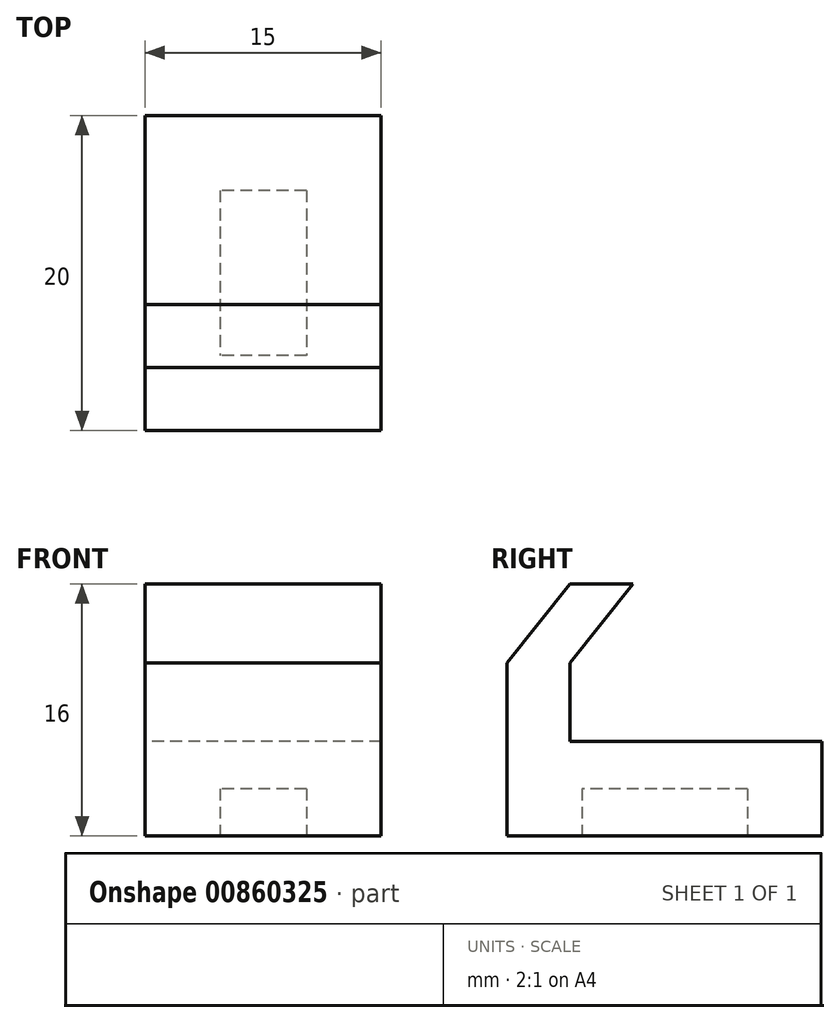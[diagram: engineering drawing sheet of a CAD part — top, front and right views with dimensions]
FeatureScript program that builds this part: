
annotation { "Feature Type Name" : "Feature", "Feature Type Description" : "" }
export const myFeature = defineFeature(function(context is Context, id is Id, definition is map)
    precondition{}
    {
        {
            var Q0;
            Q0=qCreatedBy(makeId("Top.planeOp"),FACE);
            var sketch = newSketch(context, id + "F0", { "sketchPlane" : qUnion([Q0])});
            skLineSegment(sketch, "E0.bottom", {"start": v(0, 0) * mm, "end": v(-15, 0) * mm});
            skLineSegment(sketch, "E0.top", {"start": v(0, 20) * mm, "end": v(-15, 20) * mm});
            skLineSegment(sketch, "E0.left", {"start": v(0, 0) * mm, "end": v(0, 20) * mm});
            skLineSegment(sketch, "E0.right", {"start": v(-15, 0) * mm, "end": v(-15, 20) * mm});
            skSolve(sketch);
        }
        {
            var Q0;
            Q0=makeQuery(id+"F0.imprint","IMPRINT",FACE,{"disambiguationData":[TD([[makeQuery(id+"F0.imprint","IMPRINT",EDGE,{"derivedFrom":sQuery(id+"F0.wireOp",EDGE,"E0.bottom")}),-1.0]])]});
            extrude(context, id + "F1", {"entities" : qUnion([Q0]), "depth" : 6 * mm, "offsetDistance" : 25 * mm});
        }
        {
            var Q0;
            Q0=makeQuery(id+"F1.opExtrude","CAP_FACE",FACE,{"disambiguationData":[OSD([sQuery(id+"F0.wireOp",EDGE,"E0.bottom"),sQuery(id+"F0.wireOp",EDGE,"E0.top"),sQuery(id+"F0.wireOp",EDGE,"E0.left"),sQuery(id+"F0.wireOp",EDGE,"E0.right")])],"isStart":true});
            var sketch = newSketch(context, id + "F2", { "sketchPlane" : qUnion([Q0])});
            skLineSegment(sketch, "E1.bottom", {"start": v(-4.75, -15.25) * mm, "end": v(-10.25, -15.25) * mm});
            skLineSegment(sketch, "E1.top", {"start": v(-4.75, -4.75) * mm, "end": v(-10.25, -4.75) * mm});
            skLineSegment(sketch, "E1.left", {"start": v(-4.75, -15.25) * mm, "end": v(-4.75, -4.75) * mm});
            skLineSegment(sketch, "E1.right", {"start": v(-10.25, -15.25) * mm, "end": v(-10.25, -4.75) * mm});
            skLineSegment(sketch, "E2", {"start": v(-7.5, 0) * mm, "end": v(-7.5, -4.75) * mm});
            skLineSegment(sketch, "E3", {"start": v(-7.5, -15.25) * mm, "end": v(-7.5, -20) * mm});
            skSolve(sketch);
        }
        {
            var Q0;
            {var subQ3=sQuery(id+"F2.wireOp",EDGE,"E1.left");Q0=makeQuery(id+"F2.imprint","IMPRINT",FACE,{"disambiguationData":[TD([[makeQuery(id+"F2.imprint","IMPRINT",EDGE,{"derivedFrom":subQ3}),1.0]])]});}
            extrude(context, id + "F3", {"entities" : qUnion([Q0]), "operationType" : NewBodyOperationType.REMOVE, "oppositeDirection" : true, "depth" : 3 * mm, "offsetDistance" : 25 * mm});
        }
        {
            var Q0;
            Q0=makeQuery(id+"F1.opExtrude","CAP_FACE",FACE,{"disambiguationData":[OSD([sQuery(id+"F0.wireOp",EDGE,"E0.bottom"),sQuery(id+"F0.wireOp",EDGE,"E0.top"),sQuery(id+"F0.wireOp",EDGE,"E0.left"),sQuery(id+"F0.wireOp",EDGE,"E0.right")])],"isStart":false});
            var sketch = newSketch(context, id + "F4", { "sketchPlane" : qUnion([Q0])});
            skLineSegment(sketch, "E4.bottom", {"start": v(0, 0) * mm, "end": v(-15, 0) * mm});
            skLineSegment(sketch, "E4.top", {"start": v(0, 4) * mm, "end": v(-15, 4) * mm});
            skLineSegment(sketch, "E4.left", {"start": v(0, 0) * mm, "end": v(0, 4) * mm});
            skLineSegment(sketch, "E4.right", {"start": v(-15, 0) * mm, "end": v(-15, 4) * mm});
            skSolve(sketch);
        }
        {
            var Q0;
            Q0=makeQuery(id+"F4.imprint","IMPRINT",FACE,{"disambiguationData":[TD([[makeQuery(id+"F4.imprint","IMPRINT",EDGE,{"derivedFrom":sQuery(id+"F4.wireOp",EDGE,"E4.bottom")}),-1.0]])]});
            extrude(context, id + "F5", {"entities" : qUnion([Q0]), "operationType" : NewBodyOperationType.ADD, "depth" : 5 * mm, "offsetDistance" : 25 * mm});
        }
        {
            var Q0;
            Q0=makeQuery(id+"F5.opExtrude","CAP_FACE",FACE,{"disambiguationData":[OSD([sQuery(id+"F4.wireOp",EDGE,"E4.bottom"),sQuery(id+"F4.wireOp",EDGE,"E4.top"),sQuery(id+"F4.wireOp",EDGE,"E4.left"),sQuery(id+"F4.wireOp",EDGE,"E4.right")])],"isStart":false});
            cPlane(context, id + "F6", {"entities" : qUnion([Q0]), "cplaneType" : CPlaneType.OFFSET, "offset" : 5 * mm, "width" : 150 * mm, "height" : 150 * mm});
        }
        {
            var Q0;
            Q0=qCreatedBy(id+"F6.planeOp",FACE);
            var sketch = newSketch(context, id + "F7", { "sketchPlane" : qUnion([Q0])});
            skLineSegment(sketch, "E5.bottom", {"start": v(0, 4) * mm, "end": v(-15, 4) * mm});
            skLineSegment(sketch, "E5.top", {"start": v(0, 8) * mm, "end": v(-15, 8) * mm});
            skLineSegment(sketch, "E5.left", {"start": v(0, 4) * mm, "end": v(0, 8) * mm});
            skLineSegment(sketch, "E5.right", {"start": v(-15, 4) * mm, "end": v(-15, 8) * mm});
            skSolve(sketch);
        }
        {
            var Q1;
            Q1=makeQuery(id+"F5.opExtrude","CAP_FACE",FACE,{"disambiguationData":[OSD([sQuery(id+"F4.wireOp",EDGE,"E4.bottom"),sQuery(id+"F4.wireOp",EDGE,"E4.top"),sQuery(id+"F4.wireOp",EDGE,"E4.left"),sQuery(id+"F4.wireOp",EDGE,"E4.right")])],"isStart":false});
            var Q2;
            Q2=makeQuery(id+"F7.imprint","IMPRINT",FACE,{"disambiguationData":[TD([[makeQuery(id+"F7.imprint","IMPRINT",EDGE,{"derivedFrom":sQuery(id+"F7.wireOp",EDGE,"E5.bottom")}),-1.0]])]});
            loft(context, id + "F8", {"operationType" : NewBodyOperationType.ADD, "sheetProfilesArray" : [{ "sheetProfileEntities" : qUnion([Q1]) }, { "sheetProfileEntities" : qUnion([Q2]) }]});
        }
    });
